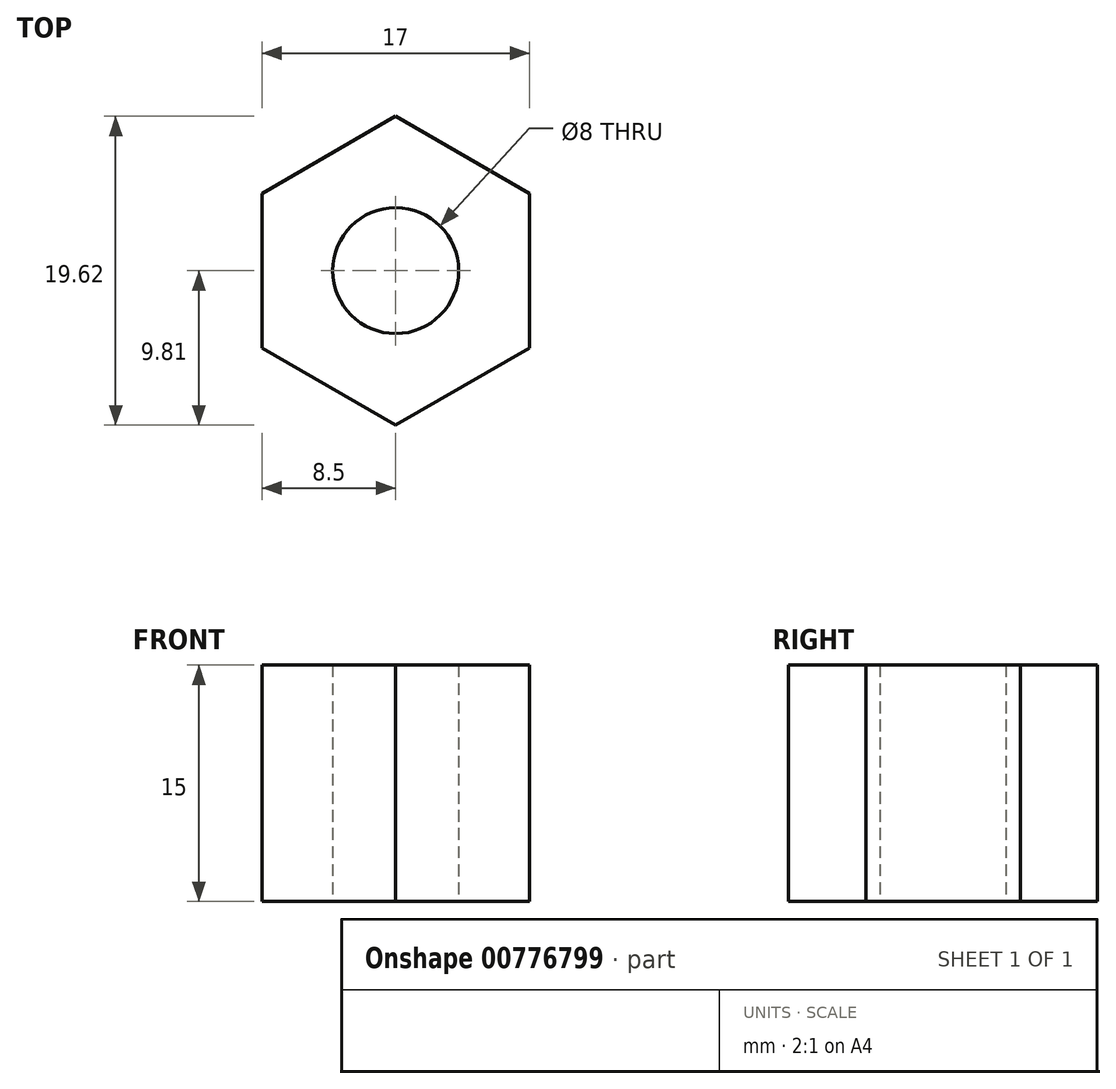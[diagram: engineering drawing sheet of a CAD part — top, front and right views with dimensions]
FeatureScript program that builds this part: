
annotation { "Feature Type Name" : "Feature", "Feature Type Description" : "" }
export const myFeature = defineFeature(function(context is Context, id is Id, definition is map)
    precondition{}
    {
        {
            var Q0;
            Q0=qCreatedBy(makeId("Top.planeOp"),FACE);
            var sketch = newSketch(context, id + "F0", { "sketchPlane" : qUnion([Q0])});
            skCircle(sketch, "E0.cCircle", {"center": v(0, 0) * mm, "radius": 8.5 * mm, "construction": true});
            skLineSegment(sketch, "E0.0", {"start": v(8.5, -4.9) * mm, "end": v(0, -9.81) * mm});
            skLineSegment(sketch, "E0.1", {"start": v(0, -9.81) * mm, "end": v(-8.5, -4.9) * mm});
            skLineSegment(sketch, "E0.2", {"start": v(-8.5, -4.9) * mm, "end": v(-8.5, 4.9) * mm});
            skLineSegment(sketch, "E0.3", {"start": v(-8.5, 4.9) * mm, "end": v(0, 9.81) * mm});
            skLineSegment(sketch, "E0.4", {"start": v(0, 9.81) * mm, "end": v(8.5, 4.9) * mm});
            skLineSegment(sketch, "E0.5", {"start": v(8.5, 4.9) * mm, "end": v(8.5, -4.9) * mm});
            skPoint(sketch, "E0.0.midPoint", {"position": v(4.25, -7.36) * mm});
            skCircle(sketch, "E1", {"center": v(0, 0) * mm, "radius": 4 * mm});
            skSolve(sketch);
        }
        {
            var Q0;
            Q0=qSketchRegion(id+"F0",true);
            extrude(context, id + "F1", {"entities" : qUnion([Q0]), "endBound" : BoundingType.SYMMETRIC, "depth" : 15 * mm});
        }
        {
            var Q0;
            Q0=makeQuery(id+"F1.opExtrude","SWEPT_BODY",BODY,{"disambiguationData":[OSD([sQuery(id+"F0.wireOp",EDGE,"E0.0"),sQuery(id+"F0.wireOp",EDGE,"E0.1"),sQuery(id+"F0.wireOp",EDGE,"E0.2"),sQuery(id+"F0.wireOp",EDGE,"E0.3"),sQuery(id+"F0.wireOp",EDGE,"E0.4"),sQuery(id+"F0.wireOp",EDGE,"E0.5"),sQuery(id+"F0.wireOp",EDGE,"E1")])]});
            transform(context, id + "F2", {"entities" : qUnion([Q0]), "transformType" : TransformType.TRANSLATION_3D, "dx" : 50 * mm, "dy" : 50 * mm, "dz" : 0 * mm, "makeCopy" : false});
        }
    });
